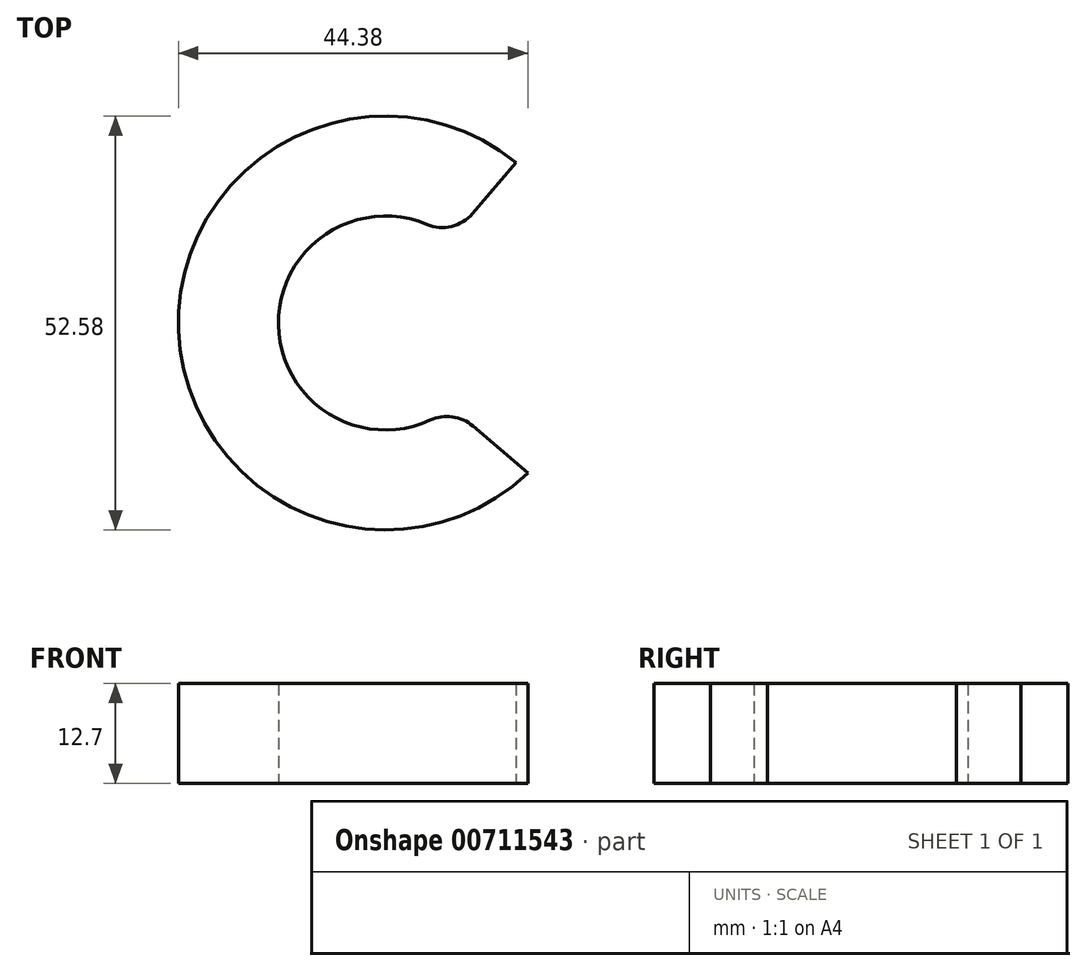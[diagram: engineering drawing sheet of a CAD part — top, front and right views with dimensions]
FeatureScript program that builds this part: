
annotation { "Feature Type Name" : "Feature", "Feature Type Description" : "" }
export const myFeature = defineFeature(function(context is Context, id is Id, definition is map)
    precondition{}
    {
        {
            var Q0;
            Q0=qCreatedBy(makeId("Top.planeOp"),FACE);
            var sketch = newSketch(context, id + "F0", { "sketchPlane" : qUnion([Q0])});
            skArc(sketch, "E0", {"start": v(8.35, 10.72) * mm, "mid": v(-13.59, 0) * mm, "end": v(8.35, -10.72) * mm});
            skArc(sketch, "E1", {"start": v(16.62, 20.37) * mm, "mid": v(-26.27, -0.98) * mm, "end": v(18.1, -19.07) * mm});
            skLineSegment(sketch, "E2", {"start": v(8.35, -10.72) * mm, "end": v(18.1, -19.07) * mm});
            skLineSegment(sketch, "E3", {"start": v(8.35, 10.72) * mm, "end": v(16.62, 20.37) * mm});
            skSolve(sketch);
        }
        {
            var Q0;
            Q0=makeQuery(id+"F0.imprint","IMPRINT",FACE,{"disambiguationData":[TD([[makeQuery(id+"F0.imprint","IMPRINT",EDGE,{"derivedFrom":sQuery(id+"F0.wireOp",EDGE,"E0")}),-1.0]])]});
            extrude(context, id + "F1", {"entities" : qUnion([Q0]), "depth" : 12.7 * mm, "offsetDistance" : 25.4 * mm});
        }
        {
            var Q0;
            Q0=makeQuery(id+"F1.opExtrude","SWEPT_EDGE",EDGE,{"disambiguationData":[OSD([sQuery(id+"F0.wireOp",EDGE,"E0"),sQuery(id+"F0.wireOp",EDGE,"E3")])]});
            var Q1;
            Q1=makeQuery(id+"F1.opExtrude","SWEPT_EDGE",EDGE,{"disambiguationData":[OSD([sQuery(id+"F0.wireOp",EDGE,"E0"),sQuery(id+"F0.wireOp",EDGE,"E2")])]});
            fillet(context, id + "F2", {"entities" : qUnion([Q0, Q1]), "radius" : 5.08 * mm, "tangentPropagation" : true, "allowEdgeOverflow" : false});
        }
    });
